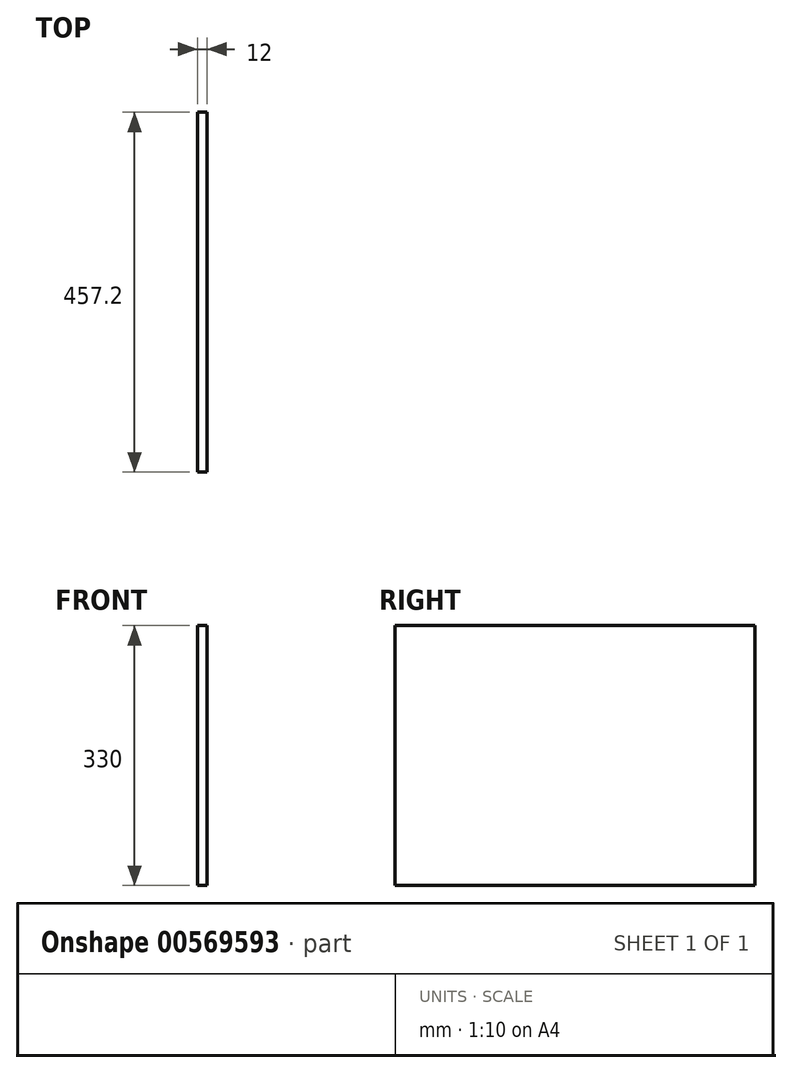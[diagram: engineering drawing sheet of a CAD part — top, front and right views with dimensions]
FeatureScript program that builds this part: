
annotation { "Feature Type Name" : "Feature", "Feature Type Description" : "" }
export const myFeature = defineFeature(function(context is Context, id is Id, definition is map)
    precondition{}
    {
        {
            var Q0;
            Q0=qCreatedBy(makeId("Top.planeOp"),FACE);
            var sketch = newSketch(context, id + "F0", { "sketchPlane" : qUnion([Q0])});
            skLineSegment(sketch, "E0.bottom", {"start": v(-48.8, 421.94) * mm, "end": v(-36.8, 421.94) * mm});
            skLineSegment(sketch, "E0.top", {"start": v(-48.8, -35.26) * mm, "end": v(-36.8, -35.26) * mm});
            skLineSegment(sketch, "E0.left", {"start": v(-48.8, 421.94) * mm, "end": v(-48.8, -35.26) * mm});
            skLineSegment(sketch, "E0.right", {"start": v(-36.8, 421.94) * mm, "end": v(-36.8, -35.26) * mm});
            skSolve(sketch);
        }
        {
            var Q0;
            Q0=makeQuery(id+"F0.imprint","IMPRINT",FACE,{"disambiguationData":[TD([[makeQuery(id+"F0.imprint","IMPRINT",EDGE,{"derivedFrom":sQuery(id+"F0.wireOp",EDGE,"E0.bottom")}),-1.0]])]});
            extrude(context, id + "F1", {"entities" : qUnion([Q0]), "depth" : 330 * mm, "offsetDistance" : 25.4 * mm});
        }
    });
